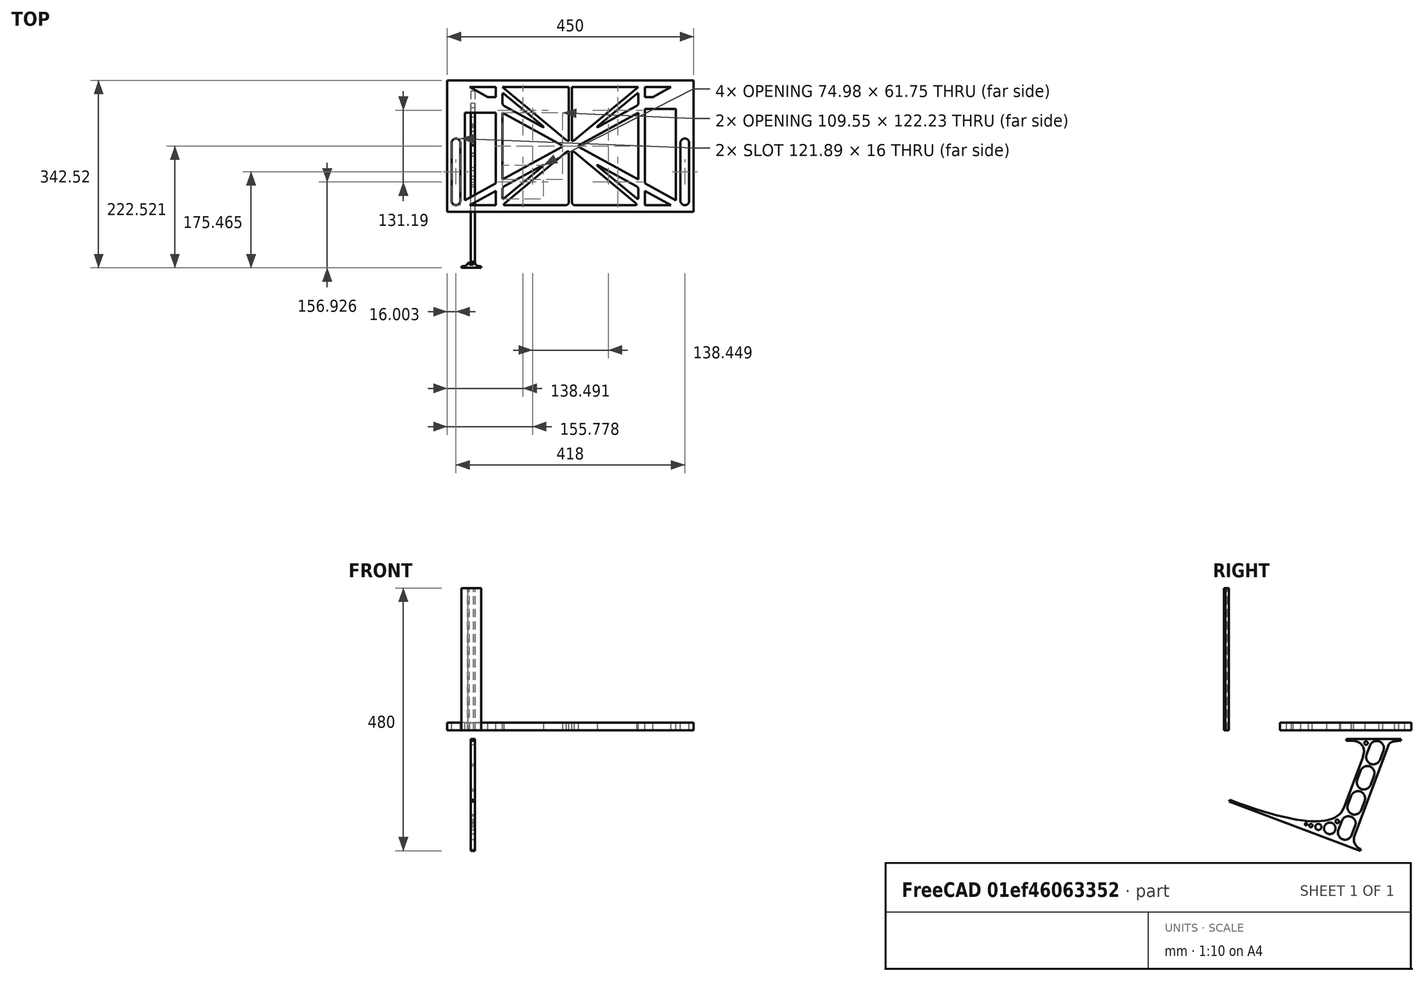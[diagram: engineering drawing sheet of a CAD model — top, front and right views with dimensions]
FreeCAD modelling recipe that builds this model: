
FCSTD DOCUMENT  (FreeCAD 0.19R0.19.2)
Label: laptopStand084
License: All rights reserved
LicenseURL: http://en.wikipedia.org/wiki/All_rights_reserved
objects: Sketcher::SketchObject×3, Part::Extrusion×3
note: 6 computed .brp shape members not serialized (recipe doc carries the construction recipe); baked Part::Feature solids carry a one-line shape summary decoded from their .brp

FEATURE [Sketcher::SketchObject] Sketch
  FullyConstrained = true
  sketch-geometry (226):
    g0: LineSegment StartX=-10.9272 StartY=-82.7794 StartZ=0 EndX=46.0728 EndY=-51.4823 EndZ=0
    g1: LineSegment StartX=366.073 StartY=-91.7794 StartZ=0 EndX=318.073 EndY=-65.424 EndZ=0
    g2: LineSegment StartX=-10.9272 StartY=77.3346 StartZ=0 EndX=-10.9272 EndY=-82.7794 EndZ=0
    g3: LineSegment StartX=375.073 StartY=-82.7794 StartZ=0 EndX=375.073 EndY=83.9235 EndZ=0
    g4: LineSegment StartX=-1.92719 StartY=-91.7794 StartZ=0 EndX=46.0728 EndY=-91.7794 EndZ=0
    g5: LineSegment StartX=318.073 StartY=124.221 StartZ=0 EndX=366.073 EndY=124.221 EndZ=0
    g6: LineSegment StartX=306.073 StartY=124.221 StartZ=0 EndX=189.124 EndY=27.0628 EndZ=0
    g7: LineSegment StartX=175.022 StartY=27.0628 StartZ=0 EndX=58.0728 EndY=124.221 EndZ=0
    g8: LineSegment StartX=306.073 StartY=77.3346 StartZ=0 EndX=306.073 EndY=-44.8935 EndZ=0
    g9: LineSegment StartX=318.073 StartY=83.9235 StartZ=0 EndX=318.073 EndY=-51.4823 EndZ=0
    g10: LineSegment StartX=318.073 StartY=-51.4823 StartZ=0 EndX=375.073 EndY=-82.7794 EndZ=0
    g11: LineSegment StartX=318.073 StartY=-65.424 StartZ=0 EndX=318.073 EndY=-91.7794 EndZ=0
    g12: LineSegment StartX=318.073 StartY=-91.7794 StartZ=0 EndX=366.073 EndY=-91.7794 EndZ=0
    g13: LineSegment StartX=58.0728 StartY=-44.8935 StartZ=0 EndX=58.0728 EndY=77.3346 EndZ=0
    g14: LineSegment StartX=46.0728 StartY=-65.424 StartZ=0 EndX=-1.92719 EndY=-91.7794 EndZ=0
    g15: LineSegment StartX=46.0728 StartY=-65.424 StartZ=0 EndX=46.0728 EndY=-91.7794 EndZ=0
    g16: LineSegment StartX=46.0728 StartY=77.3346 StartZ=0 EndX=46.0728 EndY=-51.4823 EndZ=0
    g17: LineSegment StartX=-42.9272 StartY=136.221 StartZ=0 EndX=-42.9272 EndY=-103.779 EndZ=0
    g18: LineSegment StartX=407.073 StartY=136.221 StartZ=0 EndX=407.073 EndY=-103.779 EndZ=0
    g19: LineSegment StartX=179.022 StartY=27.0628 StartZ=0 EndX=179.022 EndY=124.221 EndZ=0
    g20: LineSegment StartX=185.124 StartY=27.0628 StartZ=0 EndX=185.124 EndY=124.221 EndZ=0
    g21: ArcOfCircle CenterX=-26.9272 CenterY=22.1087 CenterZ=0 NormalX=0 NormalY=0 NormalZ=1 AngleXU=0 Radius=8 StartAngle=1e-16 EndAngle=3.14159
    g22: ArcOfCircle CenterX=-26.9272 CenterY=-83.7794 CenterZ=0 NormalX=0 NormalY=0 NormalZ=1 AngleXU=0 Radius=8 StartAngle=3.14159 EndAngle=6.28319
    g23: LineSegment StartX=-34.9272 StartY=22.1087 StartZ=0 EndX=-34.9272 EndY=-83.7794 EndZ=0
    g24: LineSegment StartX=-18.9272 StartY=22.1087 StartZ=0 EndX=-18.9272 EndY=-83.7794 EndZ=0
    g25: ArcOfCircle CenterX=391.073 CenterY=22.1087 CenterZ=0 NormalX=0 NormalY=0 NormalZ=1 AngleXU=0 Radius=8 StartAngle=-4.4e-15 EndAngle=3.14159
    g26: LineSegment StartX=399.073 StartY=22.1087 StartZ=0 EndX=399.073 EndY=-83.7794 EndZ=0
    g27: LineSegment StartX=383.073 StartY=22.1087 StartZ=0 EndX=383.073 EndY=-83.7794 EndZ=0
    g28: ArcOfCircle CenterX=391.073 CenterY=-83.7794 CenterZ=0 NormalX=0 NormalY=0 NormalZ=1 AngleXU=0 Radius=8 StartAngle=3.14159 EndAngle=6.28319
    g29: Circle CenterX=175.022 CenterY=27.0628 CenterZ=0 NormalX=0 NormalY=0 NormalZ=1 AngleXU=0 Radius=1
    g30: Circle CenterX=179.022 CenterY=24.8665 CenterZ=0 NormalX=0 NormalY=0 NormalZ=1 AngleXU=0 Radius=1
    g31: Circle CenterX=179.022 CenterY=27.0628 CenterZ=0 NormalX=0 NormalY=0 NormalZ=1 AngleXU=0 Radius=1
    g32: BSplineCurve PolesCount=3 KnotsCount=2 Degree=2 IsPeriodic=0
    g33: GeomPoint X=175.022 Y=27.0628 Z=0
    g34: GeomPoint X=179.022 Y=27.0628 Z=0
    g35: Circle CenterX=189.124 CenterY=27.0628 CenterZ=0 NormalX=0 NormalY=0 NormalZ=1 AngleXU=0 Radius=1
    g36: Circle CenterX=185.124 CenterY=24.8665 CenterZ=0 NormalX=0 NormalY=0 NormalZ=1 AngleXU=0 Radius=1
    g37: Circle CenterX=185.124 CenterY=27.0628 CenterZ=0 NormalX=0 NormalY=0 NormalZ=1 AngleXU=0 Radius=1
    g38: BSplineCurve PolesCount=3 KnotsCount=2 Degree=2 IsPeriodic=0
    g39: GeomPoint X=189.124 Y=27.0628 Z=0
    g40: GeomPoint X=185.124 Y=27.0628 Z=0
    g41: Circle CenterX=175.022 CenterY=5.37834 CenterZ=0 NormalX=0 NormalY=0 NormalZ=1 AngleXU=0 Radius=1
    g42: Circle CenterX=179.022 CenterY=7.57463 CenterZ=0 NormalX=0 NormalY=0 NormalZ=1 AngleXU=0 Radius=1
    g43: Circle CenterX=179.022 CenterY=5.34704 CenterZ=0 NormalX=0 NormalY=0 NormalZ=1 AngleXU=0 Radius=1
    g44: BSplineCurve PolesCount=3 KnotsCount=2 Degree=2 IsPeriodic=0
    g45: GeomPoint X=175.022 Y=5.37834 Z=0
    g46: GeomPoint X=179.022 Y=5.34704 Z=0
    g47: Circle CenterX=189.124 CenterY=5.37834 CenterZ=0 NormalX=0 NormalY=0 NormalZ=1 AngleXU=0 Radius=1
    g48: Circle CenterX=185.124 CenterY=7.57463 CenterZ=0 NormalX=0 NormalY=0 NormalZ=1 AngleXU=0 Radius=1
    g49: Circle CenterX=185.124 CenterY=5.34704 CenterZ=0 NormalX=0 NormalY=0 NormalZ=1 AngleXU=0 Radius=1
    g50: BSplineCurve PolesCount=3 KnotsCount=2 Degree=2 IsPeriodic=0
    g51: GeomPoint X=189.124 Y=5.37834 Z=0
    g52: GeomPoint X=185.124 Y=5.34704 Z=0
    g53: Circle CenterX=165.871 CenterY=18.1458 CenterZ=0 NormalX=0 NormalY=0 NormalZ=1 AngleXU=0 Radius=1
    g54: Circle CenterX=169.377 CenterY=16.2206 CenterZ=0 NormalX=0 NormalY=0 NormalZ=1 AngleXU=0 Radius=1
    g55: Circle CenterX=165.871 CenterY=14.2954 CenterZ=0 NormalX=0 NormalY=0 NormalZ=1 AngleXU=0 Radius=1
    g56: BSplineCurve PolesCount=3 KnotsCount=2 Degree=2 IsPeriodic=0
    g57: GeomPoint X=165.871 Y=18.1458 Z=0
    g58: GeomPoint X=165.871 Y=14.2954 Z=0
    g59: Circle CenterX=198.275 CenterY=18.1458 CenterZ=0 NormalX=0 NormalY=0 NormalZ=1 AngleXU=0 Radius=1
    g60: Circle CenterX=194.768 CenterY=16.2206 CenterZ=0 NormalX=0 NormalY=0 NormalZ=1 AngleXU=0 Radius=1
    g61: Circle CenterX=198.275 CenterY=14.2954 CenterZ=0 NormalX=0 NormalY=0 NormalZ=1 AngleXU=0 Radius=1
    g62: BSplineCurve PolesCount=3 KnotsCount=2 Degree=2 IsPeriodic=0
    g63: GeomPoint X=198.275 Y=18.1458 Z=0
    g64: GeomPoint X=198.275 Y=14.2954 Z=0
    g65: LineSegment StartX=165.871 StartY=18.1458 StartZ=0 EndX=58.0728 EndY=77.3346 EndZ=0
    g66: LineSegment StartX=58.0728 StartY=-44.8935 StartZ=0 EndX=165.871 EndY=14.2954 EndZ=0
    g67: LineSegment StartX=198.275 StartY=18.1458 StartZ=0 EndX=306.073 EndY=77.3346 EndZ=0
    g68: LineSegment StartX=198.275 StartY=14.2954 StartZ=0 EndX=306.073 EndY=-44.8935 EndZ=0
    g69: LineSegment StartX=407.073 StartY=-103.779 StartZ=0 EndX=-42.9272 EndY=-103.779 EndZ=0
    g70: LineSegment StartX=407.073 StartY=136.221 StartZ=0 EndX=-42.9272 EndY=136.221 EndZ=0
    g71: LineSegment StartX=46.0728 StartY=77.3346 StartZ=0 EndX=-10.9272 EndY=77.3346 EndZ=0
    g72: LineSegment StartX=46.0728 StartY=105.865 StartZ=0 EndX=31.5028 EndY=105.865 EndZ=0
    g73: LineSegment StartX=46.0728 StartY=124.221 StartZ=0 EndX=46.0728 EndY=105.865 EndZ=0
    g74: LineSegment StartX=-1.92719 StartY=124.221 StartZ=0 EndX=31.5028 EndY=105.865 EndZ=0
    g75: LineSegment StartX=46.0728 StartY=124.221 StartZ=0 EndX=-1.92719 EndY=124.221 EndZ=0
    g76: LineSegment StartX=318.073 StartY=83.9235 StartZ=0 EndX=375.073 EndY=83.9235 EndZ=0
    g77: LineSegment StartX=318.073 StartY=105.865 StartZ=0 EndX=332.643 EndY=105.865 EndZ=0
    g78: LineSegment StartX=332.643 StartY=105.865 StartZ=0 EndX=366.073 EndY=124.221 EndZ=0
    g79: LineSegment StartX=318.073 StartY=124.221 StartZ=0 EndX=318.073 EndY=105.865 EndZ=0
    g80: Circle CenterX=125.607 CenterY=54.1951 CenterZ=0 NormalX=0 NormalY=0 NormalZ=1 AngleXU=0 Radius=1
    g81: Circle CenterX=139.632 CenterY=46.4944 CenterZ=0 NormalX=0 NormalY=0 NormalZ=1 AngleXU=0 Radius=1
    g82: Circle CenterX=127.326 CenterY=56.7187 CenterZ=0 NormalX=0 NormalY=0 NormalZ=1 AngleXU=0 Radius=1
    g83: BSplineCurve PolesCount=3 KnotsCount=2 Degree=2 IsPeriodic=0
    g84: GeomPoint X=125.607 Y=54.1951 Z=0
    g85: GeomPoint X=127.326 Y=56.7187 Z=0
    g86: Circle CenterX=236.821 CenterY=56.7187 CenterZ=0 NormalX=0 NormalY=0 NormalZ=1 AngleXU=0 Radius=1
    g87: Circle CenterX=224.513 CenterY=46.4944 CenterZ=0 NormalX=0 NormalY=0 NormalZ=1 AngleXU=0 Radius=1
    g88: Circle CenterX=238.538 CenterY=54.1951 CenterZ=0 NormalX=0 NormalY=0 NormalZ=1 AngleXU=0 Radius=1
    g89: BSplineCurve PolesCount=3 KnotsCount=2 Degree=2 IsPeriodic=0
    g90: GeomPoint X=236.821 Y=56.7187 Z=0
    g91: GeomPoint X=238.538 Y=54.1951 Z=0
    g92: Circle CenterX=238.538 CenterY=-21.7539 CenterZ=0 NormalX=0 NormalY=0 NormalZ=1 AngleXU=0 Radius=1
    g93: Circle CenterX=224.513 CenterY=-14.0532 CenterZ=0 NormalX=0 NormalY=0 NormalZ=1 AngleXU=0 Radius=1
    g94: Circle CenterX=236.821 CenterY=-24.2775 CenterZ=0 NormalX=0 NormalY=0 NormalZ=1 AngleXU=0 Radius=1
    g95: BSplineCurve PolesCount=3 KnotsCount=2 Degree=2 IsPeriodic=0
    g96: GeomPoint X=238.538 Y=-21.7539 Z=0
    g97: GeomPoint X=236.821 Y=-24.2775 Z=0
    g98: Circle CenterX=125.607 CenterY=-21.7539 CenterZ=0 NormalX=0 NormalY=0 NormalZ=1 AngleXU=0 Radius=1
    g99: Circle CenterX=139.632 CenterY=-14.0532 CenterZ=0 NormalX=0 NormalY=0 NormalZ=1 AngleXU=0 Radius=1
    g100: Circle CenterX=127.325 CenterY=-24.2775 CenterZ=0 NormalX=0 NormalY=0 NormalZ=1 AngleXU=0 Radius=1
    g101: BSplineCurve PolesCount=3 KnotsCount=2 Degree=2 IsPeriodic=0
    g102: GeomPoint X=125.607 Y=-21.7539 Z=0
    g103: GeomPoint X=127.325 Y=-24.2775 Z=0
    g104: Circle CenterX=302.996 CenterY=111.695 CenterZ=0 NormalX=0 NormalY=0 NormalZ=1 AngleXU=0 Radius=1
    g105: Circle CenterX=306.073 CenterY=114.251 CenterZ=0 NormalX=0 NormalY=0 NormalZ=1 AngleXU=0 Radius=1
    g106: Circle CenterX=306.073 CenterY=110.251 CenterZ=0 NormalX=0 NormalY=0 NormalZ=1 AngleXU=0 Radius=1
    g107: BSplineCurve PolesCount=3 KnotsCount=2 Degree=2 IsPeriodic=0
    g108: GeomPoint X=302.996 Y=111.695 Z=0
    g109: GeomPoint X=306.073 Y=110.251 Z=0
    g110: Circle CenterX=306.073 CenterY=95.2763 CenterZ=0 NormalX=0 NormalY=0 NormalZ=1 AngleXU=0 Radius=1
    g111: Circle CenterX=306.073 CenterY=91.2763 CenterZ=0 NormalX=0 NormalY=0 NormalZ=1 AngleXU=0 Radius=1
    g112: Circle CenterX=302.567 CenterY=89.3511 CenterZ=0 NormalX=0 NormalY=0 NormalZ=1 AngleXU=0 Radius=1
    g113: BSplineCurve PolesCount=3 KnotsCount=2 Degree=2 IsPeriodic=0
    g114: GeomPoint X=306.073 Y=95.2763 Z=0
    g115: GeomPoint X=302.567 Y=89.3511 Z=0
    g116: LineSegment StartX=306.073 StartY=110.251 StartZ=0 EndX=306.073 EndY=95.2763 EndZ=0
    g117: LineSegment StartX=302.996 StartY=111.695 StartZ=0 EndX=236.821 EndY=56.7187 EndZ=0
    g118: LineSegment StartX=238.538 StartY=54.1951 StartZ=0 EndX=302.567 EndY=89.3511 EndZ=0
    g119: Circle CenterX=61.1496 CenterY=111.695 CenterZ=0 NormalX=0 NormalY=0 NormalZ=1 AngleXU=0 Radius=1
    g120: Circle CenterX=58.0728 CenterY=114.251 CenterZ=0 NormalX=0 NormalY=0 NormalZ=1 AngleXU=0 Radius=1
    g121: Circle CenterX=58.0728 CenterY=110.251 CenterZ=0 NormalX=0 NormalY=0 NormalZ=1 AngleXU=0 Radius=1
    g122: BSplineCurve PolesCount=3 KnotsCount=2 Degree=2 IsPeriodic=0
    g123: GeomPoint X=61.1496 Y=111.695 Z=0
    g124: GeomPoint X=58.0728 Y=110.251 Z=0
    g125: Circle CenterX=61.5791 CenterY=89.3511 CenterZ=0 NormalX=0 NormalY=0 NormalZ=1 AngleXU=0 Radius=1
    g126: Circle CenterX=58.0728 CenterY=91.2763 CenterZ=0 NormalX=0 NormalY=0 NormalZ=1 AngleXU=0 Radius=1
    g127: Circle CenterX=58.0728 CenterY=95.2763 CenterZ=0 NormalX=0 NormalY=0 NormalZ=1 AngleXU=0 Radius=1
    g128: BSplineCurve PolesCount=3 KnotsCount=2 Degree=2 IsPeriodic=0
    g129: GeomPoint X=61.5791 Y=89.3511 Z=0
    g130: GeomPoint X=58.0728 Y=95.2763 Z=0
    g131: LineSegment StartX=58.0728 StartY=110.251 StartZ=0 EndX=58.0728 EndY=95.2763 EndZ=0
    g132: LineSegment StartX=61.1496 StartY=111.695 StartZ=0 EndX=127.326 EndY=56.7187 EndZ=0
    g133: LineSegment StartX=125.607 StartY=54.1951 StartZ=0 EndX=61.5791 EndY=89.3511 EndZ=0
    g134: Circle CenterX=61.5791 CenterY=-56.9099 CenterZ=0 NormalX=0 NormalY=0 NormalZ=1 AngleXU=0 Radius=1
    g135: Circle CenterX=58.0728 CenterY=-58.8351 CenterZ=0 NormalX=0 NormalY=0 NormalZ=1 AngleXU=0 Radius=1
    g136: Circle CenterX=58.0728 CenterY=-62.8351 CenterZ=0 NormalX=0 NormalY=0 NormalZ=1 AngleXU=0 Radius=1
    g137: BSplineCurve PolesCount=3 KnotsCount=2 Degree=2 IsPeriodic=0
    g138: GeomPoint X=61.5791 Y=-56.9099 Z=0
    g139: GeomPoint X=58.0728 Y=-62.8351 Z=0
    g140: Circle CenterX=58.0728 CenterY=-77.8102 CenterZ=0 NormalX=0 NormalY=0 NormalZ=1 AngleXU=0 Radius=1
    g141: Circle CenterX=58.0728 CenterY=-81.8102 CenterZ=0 NormalX=0 NormalY=0 NormalZ=1 AngleXU=0 Radius=1
    g142: Circle CenterX=61.1496 CenterY=-79.2541 CenterZ=0 NormalX=0 NormalY=0 NormalZ=1 AngleXU=0 Radius=1
    g143: BSplineCurve PolesCount=3 KnotsCount=2 Degree=2 IsPeriodic=0
    g144: GeomPoint X=58.0728 Y=-77.8102 Z=0
    g145: GeomPoint X=61.1496 Y=-79.2541 Z=0
    g146: LineSegment StartX=58.0728 StartY=-62.8351 StartZ=0 EndX=58.0728 EndY=-77.8102 EndZ=0
    g147: LineSegment StartX=61.1496 StartY=-79.2541 StartZ=0 EndX=127.325 EndY=-24.2775 EndZ=0
    g148: LineSegment StartX=125.607 StartY=-21.7539 StartZ=0 EndX=61.5791 EndY=-56.9099 EndZ=0
    g149: Circle CenterX=302.567 CenterY=-56.9099 CenterZ=0 NormalX=0 NormalY=0 NormalZ=1 AngleXU=0 Radius=1
    g150: Circle CenterX=306.073 CenterY=-58.8351 CenterZ=0 NormalX=0 NormalY=0 NormalZ=1 AngleXU=0 Radius=1
    g151: Circle CenterX=306.073 CenterY=-62.8351 CenterZ=0 NormalX=0 NormalY=0 NormalZ=1 AngleXU=0 Radius=1
    g152: BSplineCurve PolesCount=3 KnotsCount=2 Degree=2 IsPeriodic=0
    g153: GeomPoint X=302.567 Y=-56.9099 Z=0
    g154: GeomPoint X=306.073 Y=-62.8351 Z=0
    g155: Circle CenterX=302.996 CenterY=-79.2541 CenterZ=0 NormalX=0 NormalY=0 NormalZ=1 AngleXU=0 Radius=1
    g156: Circle CenterX=306.073 CenterY=-81.8102 CenterZ=0 NormalX=0 NormalY=0 NormalZ=1 AngleXU=0 Radius=1
    g157: Circle CenterX=306.073 CenterY=-77.8102 CenterZ=0 NormalX=0 NormalY=0 NormalZ=1 AngleXU=0 Radius=1
    g158: BSplineCurve PolesCount=3 KnotsCount=2 Degree=2 IsPeriodic=0
    g159: GeomPoint X=302.996 Y=-79.2541 Z=0
    g160: GeomPoint X=306.073 Y=-77.8102 Z=0
    g161: LineSegment StartX=306.073 StartY=-62.8351 StartZ=0 EndX=306.073 EndY=-77.8102 EndZ=0
    g162: LineSegment StartX=302.996 StartY=-79.2541 StartZ=0 EndX=236.821 EndY=-24.2775 EndZ=0
    g163: LineSegment StartX=238.538 StartY=-21.7539 StartZ=0 EndX=302.567 EndY=-56.9099 EndZ=0
    g164: Circle CenterX=61.6457 CenterY=-88.8112 CenterZ=0 NormalX=0 NormalY=0 NormalZ=1 AngleXU=0 Radius=1
    g165: Circle CenterX=58.0728 CenterY=-91.7794 CenterZ=0 NormalX=0 NormalY=0 NormalZ=1 AngleXU=0 Radius=1
    g166: Circle CenterX=63.9135 CenterY=-91.7794 CenterZ=0 NormalX=0 NormalY=0 NormalZ=1 AngleXU=0 Radius=1
    g167: BSplineCurve PolesCount=3 KnotsCount=2 Degree=2 IsPeriodic=0
    g168: GeomPoint X=61.6457 Y=-88.8112 Z=0
    g169: GeomPoint X=63.9135 Y=-91.7794 Z=0
    g170: Circle CenterX=179.022 CenterY=-85.8163 CenterZ=0 NormalX=0 NormalY=0 NormalZ=1 AngleXU=0 Radius=1
    g171: Circle CenterX=179.022 CenterY=-91.7794 CenterZ=0 NormalX=0 NormalY=0 NormalZ=1 AngleXU=0 Radius=1
    g172: Circle CenterX=171.895 CenterY=-91.7794 CenterZ=0 NormalX=0 NormalY=0 NormalZ=1 AngleXU=0 Radius=1
    g173: BSplineCurve PolesCount=3 KnotsCount=2 Degree=2 IsPeriodic=0
    g174: GeomPoint X=179.022 Y=-85.8163 Z=0
    g175: GeomPoint X=171.895 Y=-91.7794 Z=0
    g176: Circle CenterX=185.124 CenterY=-86.2028 CenterZ=0 NormalX=0 NormalY=0 NormalZ=1 AngleXU=0 Radius=1
    g177: Circle CenterX=185.124 CenterY=-91.7794 CenterZ=0 NormalX=0 NormalY=0 NormalZ=1 AngleXU=0 Radius=1
    g178: Circle CenterX=191.747 CenterY=-91.7794 CenterZ=0 NormalX=0 NormalY=0 NormalZ=1 AngleXU=0 Radius=1
    g179: BSplineCurve PolesCount=3 KnotsCount=2 Degree=2 IsPeriodic=0
    g180: GeomPoint X=185.124 Y=-86.2028 Z=0
    g181: GeomPoint X=191.747 Y=-91.7794 Z=0
    g182: Circle CenterX=299.888 CenterY=-86.6413 CenterZ=0 NormalX=0 NormalY=0 NormalZ=1 AngleXU=0 Radius=1
    g183: Circle CenterX=306.073 CenterY=-91.7794 CenterZ=0 NormalX=0 NormalY=0 NormalZ=1 AngleXU=0 Radius=1
    g184: Circle CenterX=298.776 CenterY=-91.7794 CenterZ=0 NormalX=0 NormalY=0 NormalZ=1 AngleXU=0 Radius=1
    g185: BSplineCurve PolesCount=3 KnotsCount=2 Degree=2 IsPeriodic=0
    g186: GeomPoint X=299.888 Y=-86.6413 Z=0
    g187: GeomPoint X=298.776 Y=-91.7794 Z=0
    g188: LineSegment StartX=189.124 StartY=5.37834 StartZ=0 EndX=299.888 EndY=-86.6413 EndZ=0
    g189: LineSegment StartX=298.776 StartY=-91.7794 StartZ=0 EndX=191.747 EndY=-91.7794 EndZ=0
    g190: LineSegment StartX=185.124 StartY=-86.2028 StartZ=0 EndX=185.124 EndY=5.34704 EndZ=0
    g191: LineSegment StartX=179.022 StartY=5.34704 StartZ=0 EndX=179.022 EndY=-85.8163 EndZ=0
    g192: LineSegment StartX=171.895 StartY=-91.7794 StartZ=0 EndX=63.9135 EndY=-91.7794 EndZ=0
    g193: LineSegment StartX=61.6457 StartY=-88.8112 StartZ=0 EndX=175.022 EndY=5.37834 EndZ=0
    g194: LineSegment StartX=306.073 StartY=124.221 StartZ=0 EndX=302.996 EndY=121.665 EndZ=0
    g195: LineSegment StartX=306.073 StartY=124.221 StartZ=0 EndX=302.073 EndY=124.221 EndZ=0
    g196: LineSegment StartX=185.124 StartY=124.221 StartZ=0 EndX=189.124 EndY=124.221 EndZ=0
    g197: LineSegment StartX=185.124 StartY=124.221 StartZ=0 EndX=185.124 EndY=120.221 EndZ=0
    g198: LineSegment StartX=179.022 StartY=124.221 StartZ=0 EndX=179.022 EndY=120.221 EndZ=0
    g199: LineSegment StartX=179.022 StartY=124.221 StartZ=0 EndX=175.022 EndY=124.221 EndZ=0
    g200: LineSegment StartX=58.0728 StartY=124.221 StartZ=0 EndX=62.0728 EndY=124.221 EndZ=0
    g201: LineSegment StartX=58.0728 StartY=124.221 StartZ=0 EndX=61.1496 EndY=121.665 EndZ=0
    g202: Circle CenterX=302.073 CenterY=124.221 CenterZ=0 NormalX=0 NormalY=0 NormalZ=1 AngleXU=0 Radius=1
    g203: Circle CenterX=306.073 CenterY=124.221 CenterZ=0 NormalX=0 NormalY=0 NormalZ=1 AngleXU=0 Radius=1
    g204: Circle CenterX=302.996 CenterY=121.665 CenterZ=0 NormalX=0 NormalY=0 NormalZ=1 AngleXU=0 Radius=1
    g205: BSplineCurve PolesCount=3 KnotsCount=2 Degree=2 IsPeriodic=0
    g206: GeomPoint X=302.073 Y=124.221 Z=0
    g207: GeomPoint X=302.996 Y=121.665 Z=0
    g208: Circle CenterX=189.124 CenterY=124.221 CenterZ=0 NormalX=0 NormalY=0 NormalZ=1 AngleXU=0 Radius=1
    g209: Circle CenterX=185.124 CenterY=124.221 CenterZ=0 NormalX=0 NormalY=0 NormalZ=1 AngleXU=0 Radius=1
    g210: Circle CenterX=185.124 CenterY=120.221 CenterZ=0 NormalX=0 NormalY=0 NormalZ=1 AngleXU=0 Radius=1
    g211: BSplineCurve PolesCount=3 KnotsCount=2 Degree=2 IsPeriodic=0
    g212: GeomPoint X=189.124 Y=124.221 Z=0
    g213: GeomPoint X=185.124 Y=120.221 Z=0
    g214: Circle CenterX=175.022 CenterY=124.221 CenterZ=0 NormalX=0 NormalY=0 NormalZ=1 AngleXU=0 Radius=1
    g215: Circle CenterX=179.022 CenterY=124.221 CenterZ=0 NormalX=0 NormalY=0 NormalZ=1 AngleXU=0 Radius=1
    g216: Circle CenterX=179.022 CenterY=120.221 CenterZ=0 NormalX=0 NormalY=0 NormalZ=1 AngleXU=0 Radius=1
    g217: BSplineCurve PolesCount=3 KnotsCount=2 Degree=2 IsPeriodic=0
    g218: GeomPoint X=175.022 Y=124.221 Z=0
    g219: GeomPoint X=179.022 Y=120.221 Z=0
    g220: Circle CenterX=62.0728 CenterY=124.221 CenterZ=0 NormalX=0 NormalY=0 NormalZ=1 AngleXU=0 Radius=1
    g221: Circle CenterX=58.0728 CenterY=124.221 CenterZ=0 NormalX=0 NormalY=0 NormalZ=1 AngleXU=0 Radius=1
    g222: Circle CenterX=61.1496 CenterY=121.665 CenterZ=0 NormalX=0 NormalY=0 NormalZ=1 AngleXU=0 Radius=1
    g223: BSplineCurve PolesCount=3 KnotsCount=2 Degree=2 IsPeriodic=0
    g224: GeomPoint X=62.0728 Y=124.221 Z=0
    g225: GeomPoint X=61.1496 Y=121.665 Z=0
  constraints (405):
    c: Horizontal(g4)
    c: Horizontal(g5)
    c: Coincident(g9,g10)
    c: Coincident(g11,g1)
    c: Tangent(g9,g11)
    c: Coincident(g15,g14)
    c: Coincident(g0,g16)
    c: Block(g7)
    c: Block(g6)
    c: Block(g10)
    c: Block(g3)
    c: Block(g1)
    c: Block(g11)
    c: Block(g15)
    c: Block(g14)
    c: Block(g0)
    c: Block(g2)
    c: Block(g8)
    c: Block(g5)
    c: Block(g12)
    c: Block(g4)
    c: Vertical(g17)
    c: Vertical(g18)
    c: Block(g18)
    c: Block(g17)
    c: Vertical(g19)
    c: Vertical(g20)
    c: Block(g19)
    c: Block(g20)
    c: Tangent(g21,g24) = 1.5708
    c: Tangent(g21,g23) = -1.5708
    c: Tangent(g23,g22) = -1.5708
    c: Tangent(g24,g22) = 1.5708
    c: Vertical(g23)
    c: Equal(g21,g22)
    c: Block(g24)
    c: Block(g23)
    c: Tangent(g25,g26) = 1.5708
    c: Tangent(g26,g28) = 1.5708
    c: Equal(g25,g28)
    c: Coincident(g27,g25)
    c: Coincident(g27,g28)
    c: Block(g26)
    c: Block(g27)
    c: Coincident(g32,g7)
    c: Weight(g29) = 1
    c: Equal(g29,g30)
    c: Equal(g29,g31)
    c: Coincident(g32,g19)
    c: InternalAlignment(g29,g32)
    c: InternalAlignment(g30,g32)
    c: InternalAlignment(g31,g32)
    c: InternalAlignment(g33,g32)
    c: InternalAlignment(g34,g32)
    c: Coincident(g38,g6)
    c: Weight(g35) = 1
    c: Equal(g35,g36)
    c: Equal(g35,g37)
    c: Coincident(g38,g20)
    c: InternalAlignment(g35,g38)
    c: InternalAlignment(g36,g38)
    c: InternalAlignment(g37,g38)
    c: InternalAlignment(g39,g38)
    c: InternalAlignment(g40,g38)
    c: Block(g38)
    c: Block(g32)
    c: Weight(g41) = 1
    c: Equal(g41,g42)
    c: Equal(g41,g43)
    c: InternalAlignment(g41,g44)
    c: InternalAlignment(g42,g44)
    c: InternalAlignment(g43,g44)
    c: InternalAlignment(g45,g44)
    c: InternalAlignment(g46,g44)
    c: Weight(g47) = 1
    c: Equal(g47,g48)
    c: Equal(g47,g49)
    c: InternalAlignment(g47,g50)
    c: InternalAlignment(g48,g50)
    c: InternalAlignment(g49,g50)
    c: InternalAlignment(g51,g50)
    c: InternalAlignment(g52,g50)
    c: Block(g50)
    c: Block(g44)
    c: Weight(g53) = 1
    c: Equal(g53,g54)
    c: Equal(g53,g55)
    c: InternalAlignment(g53,g56)
    c: InternalAlignment(g54,g56)
    c: InternalAlignment(g55,g56)
    c: InternalAlignment(g57,g56)
    c: InternalAlignment(g58,g56)
    c: Weight(g59) = 1
    c: Equal(g59,g60)
    c: Equal(g59,g61)
    c: InternalAlignment(g59,g62)
    c: InternalAlignment(g60,g62)
    c: InternalAlignment(g61,g62)
    c: InternalAlignment(g63,g62)
    c: InternalAlignment(g64,g62)
    c: Block(g56)
    c: Block(g62)
    c: Coincident(g65,g56)
    c: Coincident(g65,g13)
    c: Coincident(g66,g13)
    c: Coincident(g66,g56)
    c: Coincident(g67,g62)
    c: Coincident(g67,g8)
    c: Coincident(g68,g62)
    c: Coincident(g68,g8)
    c: Block(g13)
    c: Coincident(g69,g18)
    c: Coincident(g69,g17)
    c: Horizontal(g69)
    c: Distance(g69) = 450
    c: Coincident(g70,g18)
    c: Coincident(g70,g17)
    c: Horizontal(g70)
    c: Horizontal(g71)
    c: Coincident(g16,g71)
    c: Horizontal(g72)
    c: Vertical(g73)
    c: Block(g73)
    c: Block(g72)
    c: Block(g71)
    c: Distance(g73) = 18.3554
    c: Coincident(g75,g73)
    c: Coincident(g75,g74)
    c: Horizontal(g75)
    c: Block(g75)
    c: Block(g74)
    c: Coincident(g72,g74)
    c: Coincident(g2,g71)
    c: Coincident(g76,g9)
    c: Horizontal(g76)
    c: Horizontal(g77)
    c: Block(g76)
    c: Coincident(g78,g5)
    c: Coincident(g79,g5)
    c: Coincident(g79,g77)
    c: Vertical(g79)
    c: Block(g79)
    c: Coincident(g77,g78)
    c: Block(g78)
    c: Coincident(g3,g76)
    c: Weight(g80) = 1
    c: Equal(g80,g81)
    c: Equal(g80,g82)
    c: InternalAlignment(g80,g83)
    c: InternalAlignment(g81,g83)
    c: InternalAlignment(g82,g83)
    c: InternalAlignment(g84,g83)
    c: InternalAlignment(g85,g83)
    c: Block(g83)
    c: Weight(g86) = 1
    c: Equal(g86,g87)
    c: Equal(g86,g88)
    c: InternalAlignment(g86,g89)
    c: InternalAlignment(g87,g89)
    c: InternalAlignment(g88,g89)
    c: InternalAlignment(g90,g89)
    c: InternalAlignment(g91,g89)
    c: Block(g89)
    c: Weight(g92) = 1
    c: Equal(g92,g93)
    c: Equal(g92,g94)
    c: InternalAlignment(g92,g95)
    c: InternalAlignment(g93,g95)
    c: InternalAlignment(g94,g95)
    c: InternalAlignment(g96,g95)
    c: InternalAlignment(g97,g95)
    c: Block(g95)
    c: Weight(g98) = 1
    c: Equal(g98,g99)
    c: Equal(g98,g100)
    c: InternalAlignment(g98,g101)
    c: InternalAlignment(g99,g101)
    c: InternalAlignment(g100,g101)
    c: InternalAlignment(g102,g101)
    c: InternalAlignment(g103,g101)
    c: Block(g101)
    c: Weight(g104) = 1
    c: Equal(g104,g105)
    c: Equal(g104,g106)
    c: InternalAlignment(g104,g107)
    c: InternalAlignment(g105,g107)
    c: InternalAlignment(g106,g107)
    c: InternalAlignment(g108,g107)
    c: InternalAlignment(g109,g107)
    c: Weight(g110) = 1
    c: Equal(g110,g111)
    c: Equal(g110,g112)
    c: InternalAlignment(g110,g113)
    c: InternalAlignment(g111,g113)
    c: InternalAlignment(g112,g113)
    c: InternalAlignment(g114,g113)
    c: InternalAlignment(g115,g113)
    c: Block(g107)
    c: Block(g113)
    c: Coincident(g116,g107)
    c: Coincident(g116,g113)
    c: Vertical(g116)
    c: Coincident(g117,g107)
    c: Coincident(g117,g89)
    c: Coincident(g118,g89)
    c: Coincident(g118,g113)
    c: Weight(g119) = 1
    c: Equal(g119,g120)
    c: Equal(g119,g121)
    c: InternalAlignment(g119,g122)
    c: InternalAlignment(g120,g122)
    c: InternalAlignment(g121,g122)
    c: InternalAlignment(g123,g122)
    c: InternalAlignment(g124,g122)
    c: Weight(g125) = 1
    c: Equal(g125,g126)
    c: Equal(g125,g127)
    c: InternalAlignment(g125,g128)
    c: InternalAlignment(g126,g128)
    c: InternalAlignment(g127,g128)
    c: InternalAlignment(g129,g128)
    c: InternalAlignment(g130,g128)
    c: Block(g122)
    c: Block(g128)
    c: Coincident(g131,g122)
    c: Coincident(g131,g128)
    c: Vertical(g131)
    c: Coincident(g132,g122)
    c: Coincident(g132,g83)
    c: Coincident(g133,g83)
    c: Coincident(g133,g128)
    c: Weight(g134) = 1
    c: Equal(g134,g135)
    c: Equal(g134,g136)
    c: InternalAlignment(g134,g137)
    c: InternalAlignment(g135,g137)
    c: InternalAlignment(g136,g137)
    c: InternalAlignment(g138,g137)
    c: InternalAlignment(g139,g137)
    c: Weight(g140) = 1
    c: Equal(g140,g141)
    c: Equal(g140,g142)
    c: InternalAlignment(g140,g143)
    c: InternalAlignment(g141,g143)
    c: InternalAlignment(g142,g143)
    c: InternalAlignment(g144,g143)
    c: InternalAlignment(g145,g143)
    c: Block(g137)
    c: Block(g143)
    c: Coincident(g146,g137)
    c: Coincident(g146,g143)
    c: Vertical(g146)
    c: Coincident(g147,g143)
    c: Coincident(g147,g101)
    c: Coincident(g148,g101)
    c: Coincident(g148,g137)
    c: Weight(g149) = 1
    c: Equal(g149,g150)
    c: Equal(g149,g151)
    c: InternalAlignment(g149,g152)
    c: InternalAlignment(g150,g152)
    c: InternalAlignment(g151,g152)
    c: InternalAlignment(g153,g152)
    c: InternalAlignment(g154,g152)
    c: Weight(g155) = 1
    c: Equal(g155,g156)
    c: Equal(g155,g157)
    c: InternalAlignment(g155,g158)
    c: InternalAlignment(g156,g158)
    c: InternalAlignment(g157,g158)
    c: InternalAlignment(g159,g158)
    c: InternalAlignment(g160,g158)
    c: Block(g152)
    c: Block(g158)
    c: Coincident(g161,g152)
    c: Coincident(g161,g158)
    c: Vertical(g161)
    c: Coincident(g162,g158)
    c: Coincident(g162,g95)
    c: Coincident(g163,g95)
    c: Coincident(g163,g152)
    c: Weight(g164) = 1
    c: Equal(g164,g165)
    c: Equal(g164,g166)
    c: InternalAlignment(g164,g167)
    c: InternalAlignment(g165,g167)
    c: InternalAlignment(g166,g167)
    c: InternalAlignment(g168,g167)
    c: InternalAlignment(g169,g167)
    c: Weight(g170) = 1
    c: Equal(g170,g171)
    c: Equal(g170,g172)
    c: InternalAlignment(g170,g173)
    c: InternalAlignment(g171,g173)
    c: InternalAlignment(g172,g173)
    c: InternalAlignment(g174,g173)
    c: InternalAlignment(g175,g173)
    c: Weight(g176) = 1
    c: Equal(g176,g177)
    c: Equal(g176,g178)
    c: InternalAlignment(g176,g179)
    c: InternalAlignment(g177,g179)
    c: InternalAlignment(g178,g179)
    c: InternalAlignment(g180,g179)
    c: InternalAlignment(g181,g179)
    c: Weight(g182) = 1
    c: Equal(g182,g183)
    c: Equal(g182,g184)
    c: InternalAlignment(g182,g185)
    c: InternalAlignment(g183,g185)
    c: InternalAlignment(g184,g185)
    c: InternalAlignment(g186,g185)
    c: InternalAlignment(g187,g185)
    c: Block(g185)
    c: Block(g179)
    c: Block(g173)
    c: Block(g167)
    c: Coincident(g188,g50)
    c: Coincident(g188,g185)
    c: Coincident(g189,g185)
    c: Coincident(g189,g179)
    c: Horizontal(g189)
    c: Coincident(g190,g179)
    c: Coincident(g190,g50)
    c: Vertical(g190)
    c: Coincident(g191,g44)
    c: Coincident(g191,g173)
    c: Vertical(g191)
    c: Coincident(g192,g173)
    c: Coincident(g192,g167)
    c: Horizontal(g192)
    c: Coincident(g193,g167)
    c: Coincident(g193,g44)
    c: Horizontal(g195)
    c: Horizontal(g196)
    c: Vertical(g197)
    c: Vertical(g198)
    c: Horizontal(g199)
    c: Horizontal(g200)
    c: Parallel(g201,g7)
    c: Parallel(g194,g6)
    c: Distance(g194) = 4
    c: Distance(g195) = 4
    c: Distance(g196) = 4
    c: Distance(g197) = 4
    c: Distance(g198) = 4
    c: Distance(g199) = 4
    c: Distance(g200) = 4
    c: Distance(g201) = 4
    c: Coincident(g200,g7)
    c: Coincident(g201,g7)
    c: Coincident(g198,g19)
    c: Coincident(g199,g19)
    c: Coincident(g197,g20)
    c: Coincident(g196,g20)
    c: Coincident(g194,g6)
    c: Coincident(g195,g6)
    c: Coincident(g205,g195)
    c: Weight(g202) = 1
    c: Equal(g202,g203)
    c: Coincident(g203,g6)
    c: Equal(g202,g204)
    c: Coincident(g205,g194)
    c: InternalAlignment(g202,g205)
    c: InternalAlignment(g203,g205)
    c: InternalAlignment(g204,g205)
    c: InternalAlignment(g206,g205)
    c: InternalAlignment(g207,g205)
    c: Coincident(g211,g196)
    c: Weight(g208) = 1
    c: Equal(g208,g209)
    c: Coincident(g209,g20)
    c: Equal(g208,g210)
    c: Coincident(g211,g197)
    c: InternalAlignment(g208,g211)
    c: InternalAlignment(g209,g211)
    c: InternalAlignment(g210,g211)
    c: InternalAlignment(g212,g211)
    c: InternalAlignment(g213,g211)
    c: Coincident(g217,g199)
    c: Weight(g214) = 1
    c: Equal(g214,g215)
    c: Coincident(g215,g19)
    c: Equal(g214,g216)
    c: Coincident(g217,g198)
    c: InternalAlignment(g214,g217)
    c: InternalAlignment(g215,g217)
    c: InternalAlignment(g216,g217)
    c: InternalAlignment(g218,g217)
    c: InternalAlignment(g219,g217)
    c: Coincident(g223,g200)
    c: Weight(g220) = 1
    c: Equal(g220,g221)
    c: Coincident(g221,g7)
    c: Equal(g220,g222)
    c: Coincident(g223,g201)
    c: InternalAlignment(g220,g223)
    c: InternalAlignment(g221,g223)
    c: InternalAlignment(g222,g223)
    c: InternalAlignment(g224,g223)
    c: InternalAlignment(g225,g223)
    c: Block(g223)
    c: Block(g217)
    c: Block(g211)
    c: Block(g205)
FEATURE [Sketcher::SketchObject] Sketch001
  FullyConstrained = true
  MapMode = 4
  Placement = pos=(0,0,0) rot=(0.57735,0.57735,0.57735;2.0944rad)
  Support = -> [Sketch]
  sketch-geometry (46):
    g0: BSplineCurve PolesCount=3 KnotsCount=2 Degree=2 IsPeriodic=0
    g1: ArcOfCircle CenterX=73.1223 CenterY=-32.291 CenterZ=0 NormalX=0 NormalY=0 NormalZ=1 AngleXU=0 Radius=13 StartAngle=5.92268 EndAngle=9.06428
    g2: ArcOfCircle CenterX=66.7816 CenterY=-49.1439 CenterZ=0 NormalX=0 NormalY=0 NormalZ=1 AngleXU=0 Radius=13 StartAngle=2.78068 EndAngle=5.92131
    g3: ArcOfCircle CenterX=55.9263 CenterY=-78.1807 CenterZ=0 NormalX=0 NormalY=0 NormalZ=1 AngleXU=0 Radius=13 StartAngle=5.92268 EndAngle=9.06428
    g4: ArcOfCircle CenterX=49.5884 CenterY=-95.0342 CenterZ=0 NormalX=0 NormalY=0 NormalZ=1 AngleXU=0 Radius=13 StartAngle=2.78068 EndAngle=5.92131
    g5: ArcOfCircle CenterX=38.7206 CenterY=-124.067 CenterZ=0 NormalX=0 NormalY=0 NormalZ=1 AngleXU=0 Radius=13 StartAngle=5.92268 EndAngle=9.06428
    g6: ArcOfCircle CenterX=32.3875 CenterY=-140.92 CenterZ=0 NormalX=0 NormalY=0 NormalZ=1 AngleXU=0 Radius=13 StartAngle=2.78068 EndAngle=5.92131
    g7: ArcOfCircle CenterX=21.4715 CenterY=-169.934 CenterZ=0 NormalX=0 NormalY=0 NormalZ=1 AngleXU=0 Radius=13 StartAngle=5.92268 EndAngle=9.06428
    g8: ArcOfCircle CenterX=15.1336 CenterY=-186.787 CenterZ=0 NormalX=0 NormalY=0 NormalZ=1 AngleXU=0 Radius=13 StartAngle=2.78068 EndAngle=5.92131
    g9-g12: Circle x4 (B-spline internal-alignment scaffolding for g13; pole/knot coordinates omitted)
    g13: BSplineCurve PolesCount=4 KnotsCount=2 Degree=3 IsPeriodic=0
    g14: GeomPoint X=28.8094 Y=-19.0875 Z=0
    g15: GeomPoint X=47.0443 Y=-50.4712 Z=0
    g16: Circle CenterX=53.5586 CenterY=-23.2695 CenterZ=0 NormalX=0 NormalY=0 NormalZ=1 AngleXU=0 Radius=3.24518
    g17: Circle CenterX=-195.441 CenterY=-127.082 CenterZ=0 NormalX=0 NormalY=0 NormalZ=1 AngleXU=0 Radius=1
    g18: Circle CenterX=-8.24091 CenterY=-197.481 CenterZ=0 NormalX=0 NormalY=0 NormalZ=1 AngleXU=0 Radius=1
    g19: Circle CenterX=12.8789 CenterY=-141.321 CenterZ=0 NormalX=0 NormalY=0 NormalZ=1 AngleXU=0 Radius=1
    g20: BSplineCurve PolesCount=3 KnotsCount=2 Degree=2 IsPeriodic=0
    g21: GeomPoint X=-195.441 Y=-127.082 Z=0
    g22: GeomPoint X=12.8789 Y=-141.321 Z=0
    g23: Circle CenterX=-12.8016 CenterY=-179.036 CenterZ=0 NormalX=0 NormalY=0 NormalZ=1 AngleXU=0 Radius=10.5072
    g24: Circle CenterX=0.933922 CenterY=-166.43 CenterZ=0 NormalX=0 NormalY=0 NormalZ=1 AngleXU=0 Radius=3.26661
    g25: Circle CenterX=-33.5518 CenterY=-176.44 CenterZ=0 NormalX=0 NormalY=0 NormalZ=1 AngleXU=0 Radius=5.64388
    g26: Circle CenterX=-47.2366 CenterY=-173.859 CenterZ=0 NormalX=0 NormalY=0 NormalZ=1 AngleXU=0 Radius=3.01653
    g27: Circle CenterX=-56.2595 CenterY=-171.456 CenterZ=0 NormalX=0 NormalY=0 NormalZ=1 AngleXU=0 Radius=2.12826
    g28: ArcOfCircle CenterX=51.2151 CenterY=-198.473 CenterZ=0 NormalX=0 NormalY=0 NormalZ=1 AngleXU=0 Radius=20 StartAngle=2.78189 EndAngle=4.35269
    g29: LineSegment StartX=32.4951 StartY=-191.433 StartZ=0 EndX=94.6578 EndY=-26.1352 EndZ=0
    g30: LineSegment StartX=43.1192 StartY=-220.001 StartZ=0 EndX=-196.497 EndY=-129.89 EndZ=0
    g31: LineSegment StartX=43.1192 StartY=-220.001 StartZ=0 EndX=44.1752 EndY=-217.193 EndZ=0
    g32: LineSegment StartX=117.223 StartY=-19.0875 StartZ=0 EndX=117.223 EndY=-16.0875 EndZ=0
    g33: LineSegment StartX=117.223 StartY=-16.0875 StartZ=0 EndX=17.2232 EndY=-16.0875 EndZ=0
    g34: LineSegment StartX=17.2232 StartY=-16.0875 StartZ=0 EndX=17.2232 EndY=-19.0875 EndZ=0
    g35: LineSegment StartX=28.8094 StartY=-19.0875 StartZ=0 EndX=17.2232 EndY=-19.0875 EndZ=0
    g36: LineSegment StartX=47.0443 StartY=-50.4712 StartZ=0 EndX=12.8789 EndY=-141.321 EndZ=0
    g37: LineSegment StartX=-195.441 StartY=-127.082 StartZ=0 EndX=-196.497 EndY=-129.89 EndZ=0
    g38: LineSegment StartX=85.2866 StartY=-36.8766 StartZ=0 EndX=78.9396 EndY=-53.7463 EndZ=0
    g39: LineSegment StartX=60.9579 StartY=-27.7053 StartZ=0 EndX=54.6191 EndY=-44.5532 EndZ=0
    g40: LineSegment StartX=68.0907 StartY=-82.7664 StartZ=0 EndX=61.7465 EndY=-99.6365 EndZ=0
    g41: LineSegment StartX=43.7619 StartY=-73.595 StartZ=0 EndX=37.426 EndY=-90.4435 EndZ=0
    g42: LineSegment StartX=50.885 StartY=-128.652 StartZ=0 EndX=44.5456 EndY=-145.522 EndZ=0
    g43: LineSegment StartX=26.5562 StartY=-119.481 StartZ=0 EndX=20.2251 EndY=-136.329 EndZ=0
    g44: LineSegment StartX=9.3071 StartY=-165.349 StartZ=0 EndX=2.97115 EndY=-182.197 EndZ=0
    g45: LineSegment StartX=33.6358 StartY=-174.52 StartZ=0 EndX=27.2917 EndY=-191.39 EndZ=0
  constraints (71):
    c: Block(g0)
    c: Block(g1)
    c: Block(g2)
    c: Block(g4)
    c: Block(g3)
    c: Block(g6)
    c: Block(g5)
    c: Block(g8)
    c: Block(g7)
    c: Weight(g9) = 1
    c: Equal(g9,g10)
    c: Equal(g9,g11)
    c: Equal(g9,g12)
    c: InternalAlignment(g9-g12 -> g13) x4
    c: InternalAlignment(g14,g13)
    c: InternalAlignment(g15,g13)
    c: Block(g16)
    c: Weight(g17) = 1
    c: Equal(g17,g18)
    c: Equal(g17,g19)
    c: InternalAlignment(g17,g20)
    c: InternalAlignment(g18,g20)
    c: InternalAlignment(g19,g20)
    c: InternalAlignment(g21,g20)
    c: InternalAlignment(g22,g20)
    c: Block(g20)
    c: Block(g23)
    c: Block(g24)
    c: Block(g25)
    c: Block(g26)
    c: Block(g27)
    c: Block(g28)
    c: Coincident(g29,g28)
    c: Coincident(g29,g0)
    c: Block(g13)
    c: Coincident(g31,g30)
    c: Coincident(g31,g28)
    c: Block(g31)
    c: Coincident(g32,g0)
    c: Vertical(g32)
    c: Coincident(g33,g32)
    c: Horizontal(g33)
    c: Coincident(g34,g33)
    c: Vertical(g34)
    c: Block(g33)
    c: Coincident(g35,g13)
    c: Coincident(g35,g34)
    c: Horizontal(g35)
    c: Coincident(g36,g13)
    c: Coincident(g36,g20)
    c: Coincident(g37,g20)
    c: Coincident(g37,g30)
    c: Block(g30)
    c: Coincident(g38,g1)
    c: Coincident(g38,g2)
    c: Coincident(g39,g1)
    c: Coincident(g39,g2)
    c: Coincident(g40,g3)
    c: Coincident(g40,g4)
    c: Coincident(g41,g3)
    c: Coincident(g41,g4)
    c: Coincident(g42,g5)
    c: Coincident(g42,g6)
    c: Coincident(g43,g5)
    c: Coincident(g43,g6)
    c: Coincident(g44,g7)
    c: Coincident(g44,g8)
    c: Coincident(g45,g7)
    c: Coincident(g45,g8)
    c: Distance(g30) = 256
    c: Distance(g33) = 100
FEATURE [Part::Extrusion] Extrude002
  Base = -> Sketch001
  Dir = (1,0,0)
  DirMode = 2
  FaceMakerClass = Part::FaceMakerBullseye
  LengthFwd = 8
  LengthRev = 0
  Solid = true
  Symmetric = false
FEATURE [Sketcher::SketchObject] Sketch002
  FullyConstrained = true
  sketch-geometry (20):
    g0: LineSegment StartX=-2.77179 StartY=-200.304 StartZ=0 EndX=5.22821 EndY=-200.304 EndZ=0
    g1: LineSegment StartX=5.22821 StartY=-200.304 StartZ=0 EndX=5.22821 EndY=-197.304 EndZ=0
    g2: LineSegment StartX=-2.77179 StartY=-200.304 StartZ=0 EndX=-2.77179 EndY=-197.304 EndZ=0
    g3: LineSegment StartX=5.22821 StartY=-197.304 StartZ=0 EndX=8.22821 EndY=-197.304 EndZ=0
    g4: LineSegment StartX=-2.77179 StartY=-197.304 StartZ=0 EndX=-5.77179 EndY=-197.304 EndZ=0
    g5: LineSegment StartX=19.2282 StartY=-203.304 StartZ=0 EndX=19.2282 EndY=-206.304 EndZ=0
    g6: LineSegment StartX=-16.7718 StartY=-203.304 StartZ=0 EndX=-16.7718 EndY=-206.304 EndZ=0
    g7: LineSegment StartX=-16.7718 StartY=-206.304 StartZ=0 EndX=19.2282 EndY=-206.304 EndZ=0
    g8: Circle CenterX=-16.7718 CenterY=-203.304 CenterZ=0 NormalX=0 NormalY=0 NormalZ=1 AngleXU=0 Radius=1
    g9: Circle CenterX=-5.77179 CenterY=-203.304 CenterZ=0 NormalX=0 NormalY=0 NormalZ=1 AngleXU=0 Radius=1
    g10: Circle CenterX=-5.77179 CenterY=-197.304 CenterZ=0 NormalX=0 NormalY=0 NormalZ=1 AngleXU=0 Radius=1
    g11: BSplineCurve PolesCount=3 KnotsCount=2 Degree=2 IsPeriodic=0
    g12: GeomPoint X=-16.7718 Y=-203.304 Z=0
    g13: GeomPoint X=-5.77179 Y=-197.304 Z=0
    g14: Circle CenterX=19.2282 CenterY=-203.304 CenterZ=0 NormalX=0 NormalY=0 NormalZ=1 AngleXU=0 Radius=1
    g15: Circle CenterX=8.22821 CenterY=-203.304 CenterZ=0 NormalX=0 NormalY=0 NormalZ=1 AngleXU=0 Radius=1
    g16: Circle CenterX=8.22821 CenterY=-197.304 CenterZ=0 NormalX=0 NormalY=0 NormalZ=1 AngleXU=0 Radius=1
    g17: BSplineCurve PolesCount=3 KnotsCount=2 Degree=2 IsPeriodic=0
    g18: GeomPoint X=19.2282 Y=-203.304 Z=0
    g19: GeomPoint X=8.22821 Y=-197.304 Z=0
  constraints (41):
    c: Horizontal(g0)
    c: Distance(g0) = 8
    c: Coincident(g1,g0)
    c: Vertical(g1)
    c: Distance(g1) = 3
    c: Coincident(g2,g0)
    c: Vertical(g2)
    c: Distance(g2) = 3
    c: Coincident(g3,g1)
    c: Horizontal(g3)
    c: Distance(g3) = 3
    c: Coincident(g4,g2)
    c: Horizontal(g4)
    c: Distance(g4) = 3
    c: Vertical(g5)
    c: Vertical(g6)
    c: Coincident(g7,g6)
    c: Coincident(g7,g5)
    c: Weight(g8) = 1
    c: Equal(g8,g9)
    c: Equal(g8,g10)
    c: Coincident(g11,g4)
    c: InternalAlignment(g8,g11)
    c: InternalAlignment(g9,g11)
    c: InternalAlignment(g10,g11)
    c: InternalAlignment(g12,g11)
    c: InternalAlignment(g13,g11)
    c: Coincident(g17,g5)
    c: Weight(g14) = 1
    c: Equal(g14,g15)
    c: Equal(g14,g16)
    c: Coincident(g17,g3)
    c: InternalAlignment(g14,g17)
    c: InternalAlignment(g15,g17)
    c: InternalAlignment(g16,g17)
    c: InternalAlignment(g18,g17)
    c: InternalAlignment(g19,g17)
    c: Block(g7)
    c: Block(g17)
    c: Block(g11)
    c: Block(g6)
FEATURE [Part::Extrusion] Extrude003
  Base = -> Sketch002
  Dir = (0,0,1)
  DirMode = 2
  FaceMakerClass = Part::FaceMakerBullseye
  LengthFwd = 260
  LengthRev = 0
  Solid = true
  Symmetric = false
FEATURE [Part::Extrusion] Extrude
  Base = -> Sketch
  Dir = (0,0,1)
  DirMode = 2
  FaceMakerClass = Part::FaceMakerBullseye
  LengthFwd = 14
  LengthRev = 0
  Solid = true
  Symmetric = false
